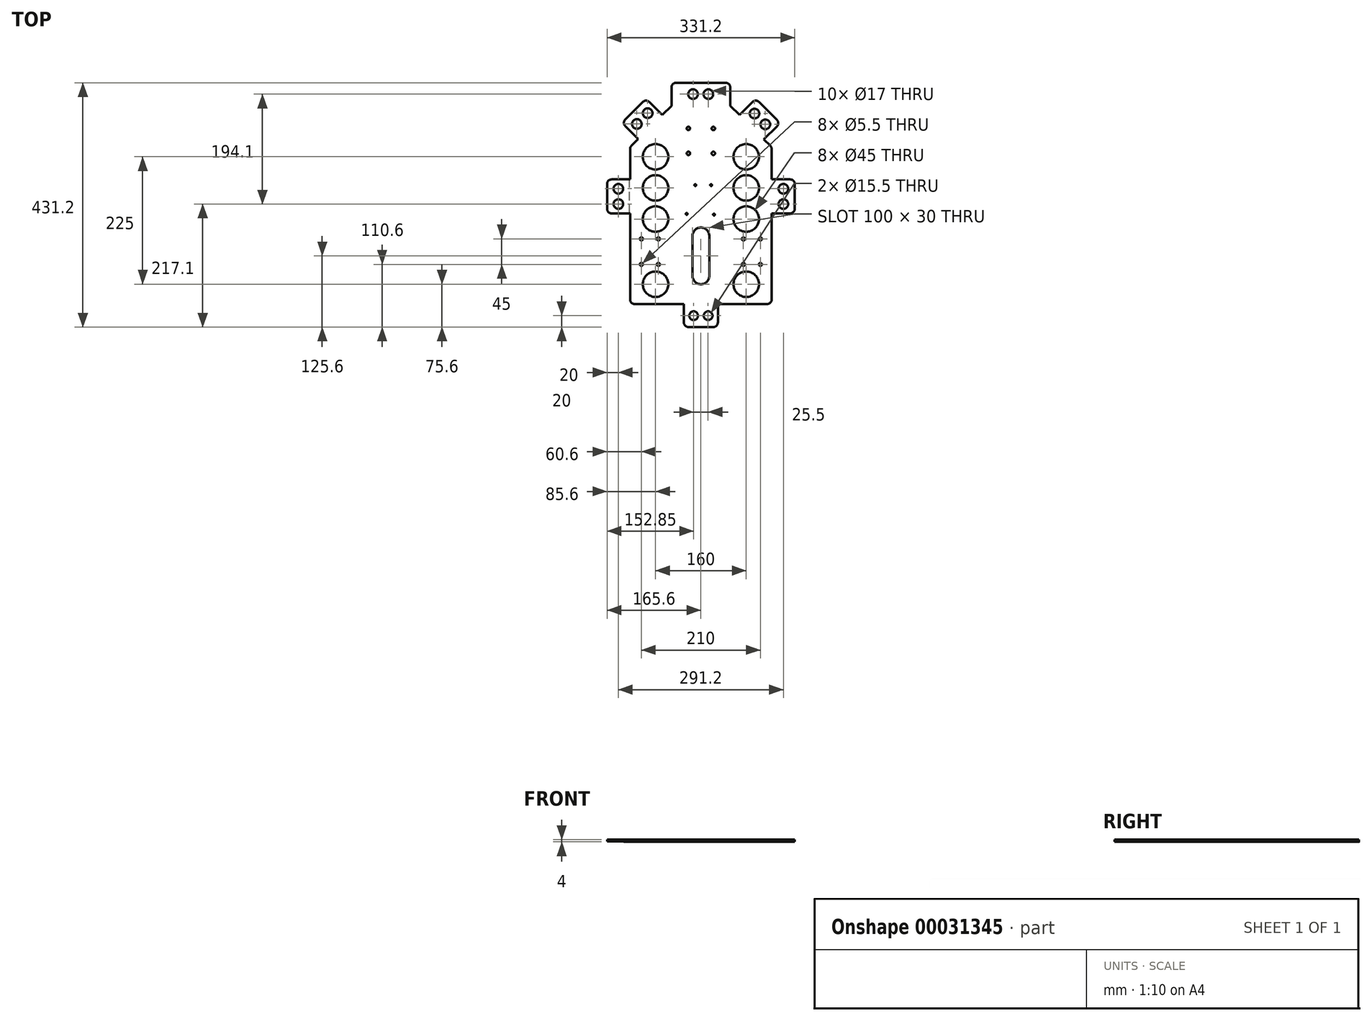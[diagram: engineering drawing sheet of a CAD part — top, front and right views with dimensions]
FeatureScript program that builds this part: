
annotation { "Feature Type Name" : "Feature", "Feature Type Description" : "" }
export const myFeature = defineFeature(function(context is Context, id is Id, definition is map)
    precondition{}
    {
        {
            var Q0;
            Q0=qCreatedBy(makeId("Top.planeOp"),FACE);
            var sketch = newSketch(context, id + "F0", { "sketchPlane" : qUnion([Q0])});
            skLineSegment(sketch, "E0.0", {"start": v(-125, -62) * mm, "end": v(-125, 90) * mm});
            skLineSegment(sketch, "E0.3", {"start": v(125, 90) * mm, "end": v(125, -62) * mm});
            skLineSegment(sketch, "E1", {"start": v(-117, -70) * mm, "end": v(-30, -70) * mm});
            skCircle(sketch, "E2.cCircle", {"center": v(0, 155) * mm, "radius": 125 * mm, "construction": true});
            skLineSegment(sketch, "E2.0", {"start": v(125, 203.46) * mm, "end": v(125, 150) * mm});
            skLineSegment(sketch, "E2.4", {"start": v(-125, 150) * mm, "end": v(-125, 203.46) * mm});
            skLineSegment(sketch, "E2.5", {"start": v(-122.66, 209.12) * mm, "end": v(-51.78, 280) * mm, "construction": true});
            skLineSegment(sketch, "E2.6", {"start": v(-51.78, 280) * mm, "end": v(51.78, 280) * mm, "construction": true});
            skLineSegment(sketch, "E2.7", {"start": v(51.78, 280) * mm, "end": v(125, 206.78) * mm, "construction": true});
            skLineSegment(sketch, "E3", {"start": v(134.23, 254.97) * mm, "end": v(102.4, 286.79) * mm});
            skLineSegment(sketch, "E4", {"start": v(43.78, 320.6) * mm, "end": v(-43.78, 320.6) * mm});
            skLineSegment(sketch, "E5", {"start": v(-51.78, 312.6) * mm, "end": v(-51.78, 280) * mm});
            skLineSegment(sketch, "E6.top", {"start": v(-22, -110.6) * mm, "end": v(22, -110.6) * mm});
            skLineSegment(sketch, "E6.left", {"start": v(-30, -70) * mm, "end": v(-30, -102.6) * mm});
            skLineSegment(sketch, "E6.right", {"start": v(30, -70) * mm, "end": v(30, -102.6) * mm});
            skLineSegment(sketch, "E7.bottom", {"start": v(-125, 150) * mm, "end": v(-157.6, 150) * mm});
            skLineSegment(sketch, "E7.top", {"start": v(-125, 90) * mm, "end": v(-157.6, 90) * mm});
            skLineSegment(sketch, "E7.right", {"start": v(-165.6, 142) * mm, "end": v(-165.6, 98) * mm});
            skLineSegment(sketch, "E8.MirrorCS", {"start": v(125, 150) * mm, "end": v(157.6, 150) * mm});
            skLineSegment(sketch, "E9.MirrorCS", {"start": v(165.6, 142) * mm, "end": v(165.6, 98) * mm});
            skLineSegment(sketch, "E10.MirrorCS", {"start": v(125, 90) * mm, "end": v(157.6, 90) * mm});
            skLineSegment(sketch, "E11", {"start": v(134.23, 243.65) * mm, "end": v(111.17, 220.6) * mm});
            skLineSegment(sketch, "E12", {"start": v(111.17, 220.6) * mm, "end": v(122.66, 209.12) * mm});
            skLineSegment(sketch, "E13", {"start": v(91.1, 286.79) * mm, "end": v(68.04, 263.74) * mm});
            skLineSegment(sketch, "E14", {"start": v(68.04, 263.74) * mm, "end": v(51.78, 280) * mm});
            skLineSegment(sketch, "E15", {"start": v(-122.66, 209.12) * mm, "end": v(-110.47, 221.31) * mm});
            skLineSegment(sketch, "E16", {"start": v(-110.47, 221.31) * mm, "end": v(-133.52, 244.36) * mm});
            skLineSegment(sketch, "E17", {"start": v(-51.78, 280) * mm, "end": v(-68.04, 263.74) * mm});
            skLineSegment(sketch, "E18", {"start": v(-68.04, 263.74) * mm, "end": v(-91.1, 286.79) * mm});
            skLineSegment(sketch, "E19", {"start": v(-133.52, 255.68) * mm, "end": v(-102.4, 286.79) * mm});
            skArc(sketch, "E20", {"start": v(-122.66, 209.12) * mm, "mid": v(-124.4, 206.52) * mm, "end": v(-125, 203.46) * mm});
            skArc(sketch, "E21", {"start": v(-133.52, 255.68) * mm, "mid": v(-135.86, 250.02) * mm, "end": v(-133.52, 244.36) * mm});
            skArc(sketch, "E22", {"start": v(-91.1, 286.79) * mm, "mid": v(-96.75, 289.13) * mm, "end": v(-102.4, 286.79) * mm});
            skArc(sketch, "E23", {"start": v(-43.78, 320.6) * mm, "mid": v(-49.43, 318.26) * mm, "end": v(-51.78, 312.6) * mm});
            skArc(sketch, "E24", {"start": v(102.4, 286.79) * mm, "mid": v(96.75, 289.13) * mm, "end": v(91.1, 286.79) * mm});
            skArc(sketch, "E25", {"start": v(157.6, 90) * mm, "mid": v(163.26, 92.34) * mm, "end": v(165.6, 98) * mm});
            skPoint(sketch, "E26.orphan", {"position": v(165.6, 90) * mm});
            skArc(sketch, "E27", {"start": v(-157.6, 150) * mm, "mid": v(-163.26, 147.66) * mm, "end": v(-165.6, 142) * mm});
            skArc(sketch, "E28", {"start": v(-165.6, 98) * mm, "mid": v(-163.26, 92.34) * mm, "end": v(-157.6, 90) * mm});
            skPoint(sketch, "E29.orphan", {"position": v(-165.6, 90) * mm});
            skPoint(sketch, "E30.orphan", {"position": v(-165.6, 150) * mm});
            skArc(sketch, "E31", {"start": v(-125, -62) * mm, "mid": v(-122.66, -67.66) * mm, "end": v(-117, -70) * mm});
            skArc(sketch, "E32.trimOffspring", {"start": v(117, -70) * mm, "mid": v(122.66, -67.66) * mm, "end": v(125, -62) * mm});
            skPoint(sketch, "E33.orphan", {"position": v(-125, -70) * mm});
            skArc(sketch, "E34", {"start": v(-30, -102.6) * mm, "mid": v(-27.66, -108.26) * mm, "end": v(-22, -110.6) * mm});
            skArc(sketch, "E35", {"start": v(22, -110.6) * mm, "mid": v(27.66, -108.26) * mm, "end": v(30, -102.6) * mm});
            skLineSegment(sketch, "E36", {"start": v(51.78, 280) * mm, "end": v(51.78, 312.6) * mm});
            skLineSegment(sketch, "E37.trimOffspring", {"start": v(30, -70) * mm, "end": v(117, -70) * mm});
            skPoint(sketch, "E38.visualSharp", {"position": v(139.88, 249.31) * mm});
            skArc(sketch, "E38.filletArc", {"start": v(134.23, 243.65) * mm, "mid": v(136.57, 249.31) * mm, "end": v(134.23, 254.97) * mm});
            skPoint(sketch, "E39.visualSharp", {"position": v(125, 206.78) * mm});
            skArc(sketch, "E39.filletArc", {"start": v(125, 203.46) * mm, "mid": v(124.4, 206.52) * mm, "end": v(122.66, 209.12) * mm});
            skPoint(sketch, "E40.visualSharp", {"position": v(165.6, 150) * mm});
            skArc(sketch, "E40.filletArc", {"start": v(165.6, 142) * mm, "mid": v(163.26, 147.66) * mm, "end": v(157.6, 150) * mm});
            skPoint(sketch, "E41.visualSharp", {"position": v(51.78, 320.6) * mm});
            skArc(sketch, "E41.filletArc", {"start": v(51.78, 312.6) * mm, "mid": v(49.43, 318.26) * mm, "end": v(43.78, 320.6) * mm});
            skSolve(sketch);
        }
        {
            var Q0;
            Q0 = qSketchRegion(id + "F0", true);
            extrude(context, id + "F1", {"entities" : qUnion([Q0]), "depth" : 4 * mm});
        }
        {
            var Q0;
            Q0=makeQuery(id+"F1.opExtrude","CAP_FACE",FACE,{"disambiguationData":[OSD([sQuery(id+"F0.wireOp",EDGE,"E0.0"),sQuery(id+"F0.wireOp",EDGE,"E0.3"),sQuery(id+"F0.wireOp",EDGE,"E0.4"),sQuery(id+"F0.wireOp",EDGE,"E0.5"),sQuery(id+"F0.wireOp",EDGE,"fc92078c-8e71-458a-bd1e-c939145f4196"),sQuery(id+"F0.wireOp",EDGE,"4c2cfc39-f78c-4514-94e9-821f44e9b5e8"),sQuery(id+"F0.wireOp",EDGE,"24fc19e9-c8c4-49f8-94e1-014fd037f0ac"),sQuery(id+"F0.wireOp",EDGE,"73de339b-9233-4791-b387-9009b4e0bfa6"),sQuery(id+"F0.wireOp",EDGE,"2889238f-878a-4334-a808-6809738859e7"),sQuery(id+"F0.wireOp",EDGE,"a27c6b49-6c67-45f8-8fd3-b383bbe31656"),sQuery(id+"F0.wireOp",EDGE,"ad68f3b6-ef5c-4002-8b56-81c0ba8a5018.trimOffspring")])],"isStart":false});
            var sketch = newSketch(context, id + "F2", { "sketchPlane" : qUnion([Q0])});
            skCircle(sketch, "E42", {"center": v(-105, 0) * mm, "radius": 2.75 * mm});
            skCircle(sketch, "E43", {"center": v(-75, 45) * mm, "radius": 2.75 * mm});
            skCircle(sketch, "E44", {"center": v(-105, 45) * mm, "radius": 2.75 * mm});
            skCircle(sketch, "E45", {"center": v(-75, 0) * mm, "radius": 2.75 * mm});
            skCircle(sketch, "E46.MirrorC", {"center": v(75, 45) * mm, "radius": 2.75 * mm});
            skCircle(sketch, "E47.MirrorC", {"center": v(75, 0) * mm, "radius": 2.75 * mm});
            skCircle(sketch, "E48.MirrorC", {"center": v(105, 0) * mm, "radius": 2.75 * mm});
            skCircle(sketch, "E49.MirrorC", {"center": v(105, 45) * mm, "radius": 2.75 * mm});
            skCircle(sketch, "E50", {"center": v(-25, 89.2) * mm, "radius": 1.6 * mm});
            skCircle(sketch, "E51", {"center": v(-9.8, 140) * mm, "radius": 1.6 * mm});
            skCircle(sketch, "E52", {"center": v(18.1, 140) * mm, "radius": 1.6 * mm});
            skCircle(sketch, "E53", {"center": v(23.2, 87.9) * mm, "radius": 1.6 * mm});
            skLineSegment(sketch, "E54", {"start": v(-41.65, 140) * mm, "end": v(24.6, 140) * mm, "construction": true});
            skCircle(sketch, "E55", {"center": v(-113.01, 247.9) * mm, "radius": 8.5 * mm});
            skCircle(sketch, "E56", {"center": v(-93.92, 266.99) * mm, "radius": 8.5 * mm});
            skCircle(sketch, "E57", {"center": v(-13.78, 300.6) * mm, "radius": 8.5 * mm});
            skCircle(sketch, "E58", {"center": v(13.22, 300.6) * mm, "radius": 8.5 * mm});
            skCircle(sketch, "E59", {"center": v(94.63, 266.28) * mm, "radius": 8.5 * mm});
            skCircle(sketch, "E60", {"center": v(113.72, 247.2) * mm, "radius": 8.5 * mm});
            skCircle(sketch, "E61", {"center": v(-12.75, -90.6) * mm, "radius": 7.75 * mm});
            skCircle(sketch, "E62", {"center": v(12.75, -90.6) * mm, "radius": 7.75 * mm});
            skCircle(sketch, "E63", {"center": v(-22, 240) * mm, "radius": 3 * mm});
            skCircle(sketch, "E64", {"center": v(22, 240) * mm, "radius": 3 * mm});
            skCircle(sketch, "E65", {"center": v(22, 196) * mm, "radius": 3 * mm});
            skCircle(sketch, "E66", {"center": v(-22, 196) * mm, "radius": 3 * mm});
            skCircle(sketch, "E67", {"center": v(-145.6, 133.5) * mm, "radius": 8.5 * mm});
            skCircle(sketch, "E68", {"center": v(-145.6, 106.5) * mm, "radius": 8.5 * mm});
            skCircle(sketch, "E69.MirrorC", {"center": v(145.6, 133.5) * mm, "radius": 8.5 * mm});
            skCircle(sketch, "E70.MirrorC", {"center": v(145.6, 106.5) * mm, "radius": 8.5 * mm});
            skCircle(sketch, "E71", {"center": v(-80, 190) * mm, "radius": 22.5 * mm});
            skCircle(sketch, "E72", {"center": v(-80, 135) * mm, "radius": 22.5 * mm});
            skCircle(sketch, "E73", {"center": v(-80, 80) * mm, "radius": 22.5 * mm});
            skCircle(sketch, "E74", {"center": v(80, 190) * mm, "radius": 22.5 * mm});
            skCircle(sketch, "E75", {"center": v(80, 135) * mm, "radius": 22.5 * mm});
            skCircle(sketch, "E76", {"center": v(80, 80) * mm, "radius": 22.5 * mm});
            skCircle(sketch, "E77", {"center": v(80, -35) * mm, "radius": 22.5 * mm});
            skCircle(sketch, "E78", {"center": v(-80, -35) * mm, "radius": 22.5 * mm});
            skLineSegment(sketch, "E79", {"start": v(-80, 340.13) * mm, "end": v(-80, -152.86) * mm, "construction": true});
            skLineSegment(sketch, "E80", {"start": v(80, 340.04) * mm, "end": v(80, -137.54) * mm, "construction": true});
            skSolve(sketch);
        }
        {
            var Q0;
            Q0 = qSketchRegion(id + "F2", true);
            extrude(context, id + "F3", {"entities" : qUnion([Q0]), "operationType" : NewBodyOperationType.REMOVE, "endBound" : BoundingType.UP_TO_NEXT, "oppositeDirection" : true, "depth" : 25 * mm});
        }
        {
            var Q0;
            Q0=makeQuery(id+"F1.opExtrude","CAP_FACE",FACE,{"disambiguationData":[OSD([sQuery(id+"F0.wireOp",EDGE,"E0.0"),sQuery(id+"F0.wireOp",EDGE,"E0.3"),sQuery(id+"F0.wireOp",EDGE,"E0.4"),sQuery(id+"F0.wireOp",EDGE,"E0.5"),sQuery(id+"F0.wireOp",EDGE,"fc92078c-8e71-458a-bd1e-c939145f4196"),sQuery(id+"F0.wireOp",EDGE,"4c2cfc39-f78c-4514-94e9-821f44e9b5e8"),sQuery(id+"F0.wireOp",EDGE,"24fc19e9-c8c4-49f8-94e1-014fd037f0ac"),sQuery(id+"F0.wireOp",EDGE,"73de339b-9233-4791-b387-9009b4e0bfa6"),sQuery(id+"F0.wireOp",EDGE,"2889238f-878a-4334-a808-6809738859e7"),sQuery(id+"F0.wireOp",EDGE,"a27c6b49-6c67-45f8-8fd3-b383bbe31656"),sQuery(id+"F0.wireOp",EDGE,"ad68f3b6-ef5c-4002-8b56-81c0ba8a5018.trimOffspring")])],"isStart":false});
            var sketch = newSketch(context, id + "F4", { "sketchPlane" : qUnion([Q0])});
            skLineSegment(sketch, "E81.left", {"start": v(-15, 50) * mm, "end": v(-15, -20) * mm});
            skLineSegment(sketch, "E81.right", {"start": v(15, 50) * mm, "end": v(15, -20) * mm});
            skArc(sketch, "E82", {"start": v(15, 50) * mm, "mid": v(0, 65) * mm, "end": v(-15, 50) * mm});
            skArc(sketch, "E83", {"start": v(-15, -20) * mm, "mid": v(0, -35) * mm, "end": v(15, -20) * mm});
            skSolve(sketch);
        }
        {
            var Q0;
            Q0 = qSketchRegion(id + "F4", true);
            extrude(context, id + "F5", {"entities" : qUnion([Q0]), "operationType" : NewBodyOperationType.REMOVE, "oppositeDirection" : true, "depth" : 25 * mm});
        }
        {
            var Q0;
            Q0=makeQuery(id+"F0.imprint","IMPRINT",FACE,{"disambiguationData":[TD([[makeQuery(id+"F0.imprint","IMPRINT",EDGE,{"derivedFrom":sQuery(id+"F0.wireOp",EDGE,"E0.0")}),-1.0]])]});
            var sketch = newSketch(context, id + "F6", { "sketchPlane" : qUnion([Q0])});
            skLineSegment(sketch, "E84.bottom", {"start": v(-126, 90) * mm, "end": v(-165.6, 90) * mm});
            skLineSegment(sketch, "E84.top", {"start": v(-126, 150.37) * mm, "end": v(-165.6, 150.37) * mm});
            skLineSegment(sketch, "E84.left", {"start": v(-126, 90) * mm, "end": v(-126, 150.37) * mm});
            skLineSegment(sketch, "E84.right", {"start": v(-165.6, 90) * mm, "end": v(-165.6, 150.37) * mm});
            skSolve(sketch);
        }
        {
            var Q0;
            Q0 = qSketchRegion(id + "F6", true);
            extrude(context, id + "F7", {"entities" : qUnion([Q0]), "operationType" : NewBodyOperationType.REMOVE, "depth" : 1 * mm});
        }
    });
